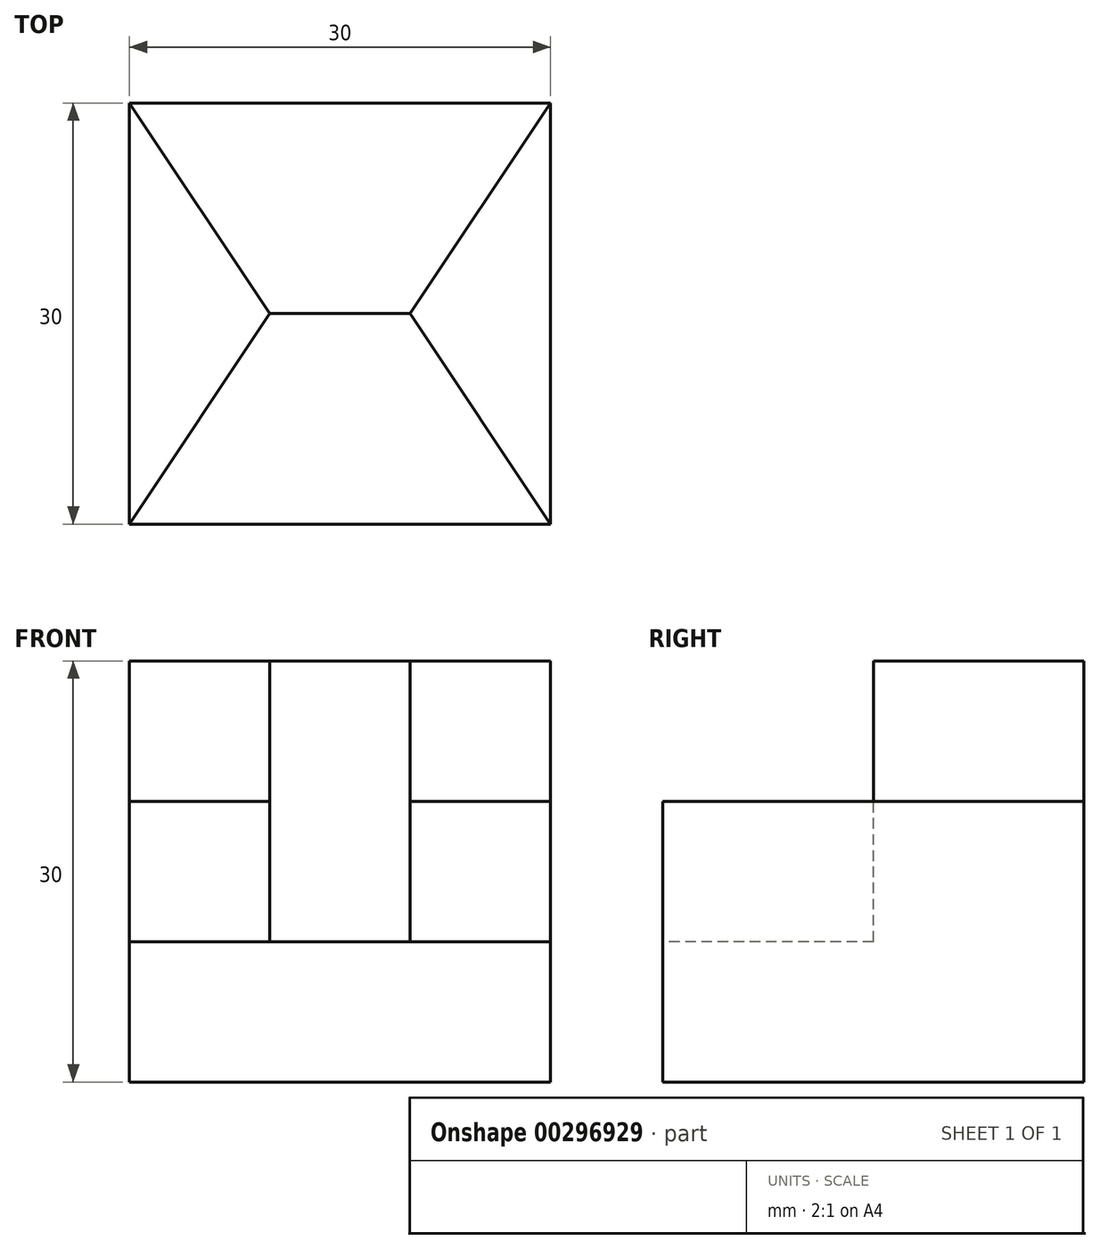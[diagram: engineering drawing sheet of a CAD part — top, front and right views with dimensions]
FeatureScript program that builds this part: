
annotation { "Feature Type Name" : "Feature", "Feature Type Description" : "" }
export const myFeature = defineFeature(function(context is Context, id is Id, definition is map)
    precondition{}
    {
        {
            var Q0;
            Q0=qCreatedBy(makeId("Top.planeOp"),FACE);
            var sketch = newSketch(context, id + "F0", { "sketchPlane" : qUnion([Q0])});
            skLineSegment(sketch, "E0.bottom", {"start": v(0, 0) * mm, "end": v(30, 0) * mm});
            skLineSegment(sketch, "E0.top", {"start": v(0, 30) * mm, "end": v(30, 30) * mm});
            skLineSegment(sketch, "E0.left", {"start": v(0, 0) * mm, "end": v(0, 30) * mm});
            skLineSegment(sketch, "E0.right", {"start": v(30, 0) * mm, "end": v(30, 30) * mm});
            skLineSegment(sketch, "E1", {"start": v(0, 30) * mm, "end": v(10, 15) * mm});
            skLineSegment(sketch, "E2", {"start": v(10, 15) * mm, "end": v(0, 0) * mm});
            skLineSegment(sketch, "E3", {"start": v(10, 15) * mm, "end": v(20, 15) * mm});
            skLineSegment(sketch, "E4", {"start": v(20, 15) * mm, "end": v(30, 30) * mm});
            skLineSegment(sketch, "E5", {"start": v(20, 15) * mm, "end": v(30, 0) * mm});
            skSolve(sketch);
        }
        {
            var Q0;
            Q0 = qSketchRegion(id + "F0", true);
            extrude(context, id + "F1", {"entities" : qUnion([Q0]), "oppositeDirection" : true, "depth" : 30 * mm});
        }
        {
            var Q0;
            Q0=makeQuery(id+"F0.imprint","IMPRINT",FACE,{"disambiguationData":[TD([[makeQuery(id+"F0.imprint","IMPRINT",EDGE,{"derivedFrom":sQuery(id+"F0.wireOp",EDGE,"E0.bottom")}),1.0]])]});
            extrude(context, id + "F2", {"entities" : qUnion([Q0]), "operationType" : NewBodyOperationType.REMOVE, "oppositeDirection" : true, "depth" : 20 * mm});
        }
        {
            var Q0;
            Q0=makeQuery(id+"F0.imprint","IMPRINT",FACE,{"disambiguationData":[TD([[makeQuery(id+"F0.imprint","IMPRINT",EDGE,{"derivedFrom":sQuery(id+"F0.wireOp",EDGE,"E0.left")}),-1.0]])]});
            var Q1;
            Q1=makeQuery(id+"F0.imprint","IMPRINT",FACE,{"disambiguationData":[TD([[makeQuery(id+"F0.imprint","IMPRINT",EDGE,{"derivedFrom":sQuery(id+"F0.wireOp",EDGE,"E0.right")}),1.0]])]});
            extrude(context, id + "F3", {"entities" : qUnion([Q0, Q1]), "operationType" : NewBodyOperationType.REMOVE, "oppositeDirection" : true, "depth" : 10 * mm});
        }
    });
